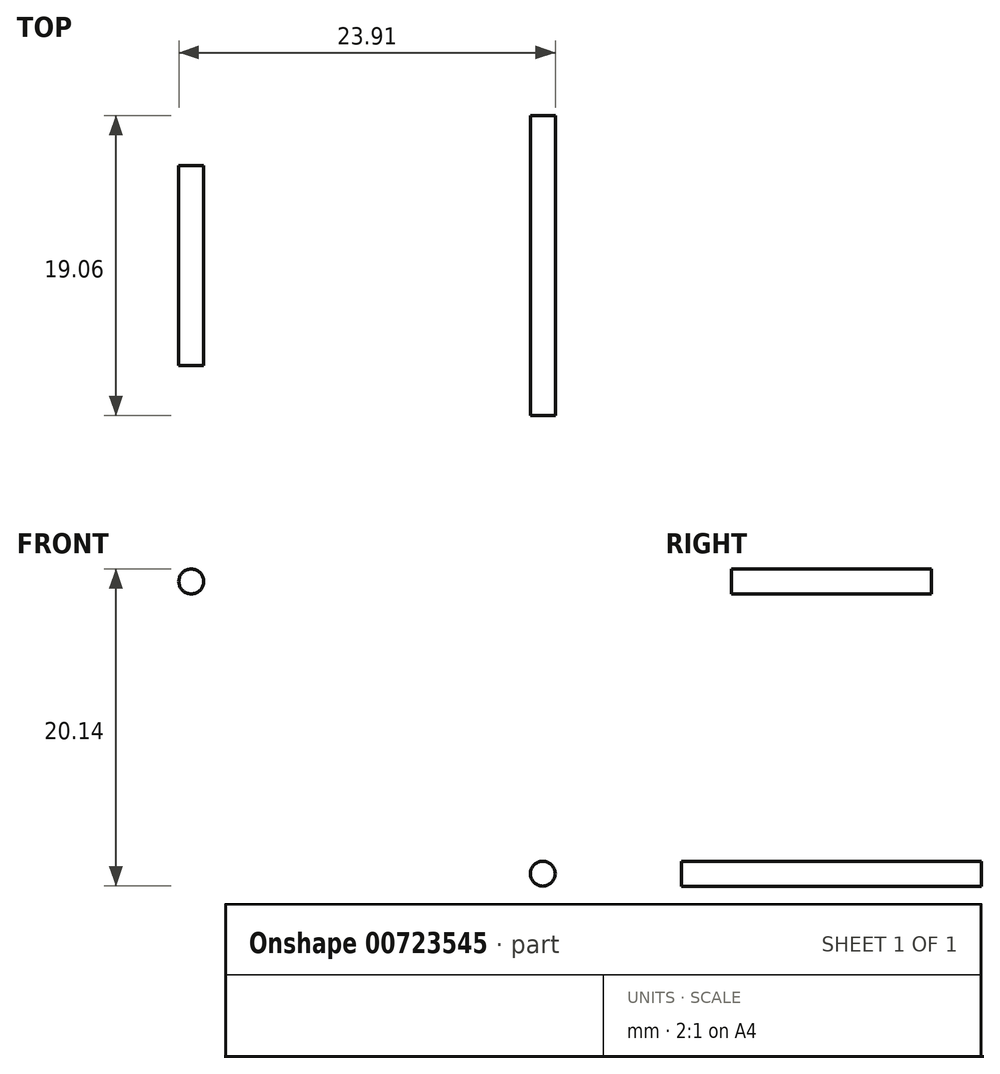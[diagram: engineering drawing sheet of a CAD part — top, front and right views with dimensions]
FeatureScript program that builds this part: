
annotation { "Feature Type Name" : "Feature", "Feature Type Description" : "" }
export const myFeature = defineFeature(function(context is Context, id is Id, definition is map)
    precondition{}
    {
        {
            var Q0;
            Q0=qCreatedBy(makeId("Front.planeOp"),FACE);
            var sketch = newSketch(context, id + "F0", { "sketchPlane" : qUnion([Q0])});
            skCircle(sketch, "E0", {"center": v(-22.1, 13.92) * mm, "radius": 0.8 * mm});
            skSolve(sketch);
        }
        {
            var Q0;
            Q0 = qSketchRegion(id + "F0", true);
            extrude(context, id + "F1", {"entities" : qUnion([Q0]), "endBound" : BoundingType.SYMMETRIC, "depth" : 19.05 * mm, "offsetDistance" : 25.4 * mm});
        }
        {
            var Q0;
            Q0=qCreatedBy(makeId("Front.planeOp"),FACE);
            var sketch = newSketch(context, id + "F2", { "sketchPlane" : qUnion([Q0])});
            skCircle(sketch, "E1", {"center": v(-44.43, 32.48) * mm, "radius": 0.8 * mm});
            skSolve(sketch);
        }
        {
            var Q0;
            Q0 = qSketchRegion(id + "F2", true);
            extrude(context, id + "F3", {"entities" : qUnion([Q0]), "endBound" : BoundingType.SYMMETRIC, "depth" : 12.7 * mm, "offsetDistance" : 25.4 * mm});
        }
    });
